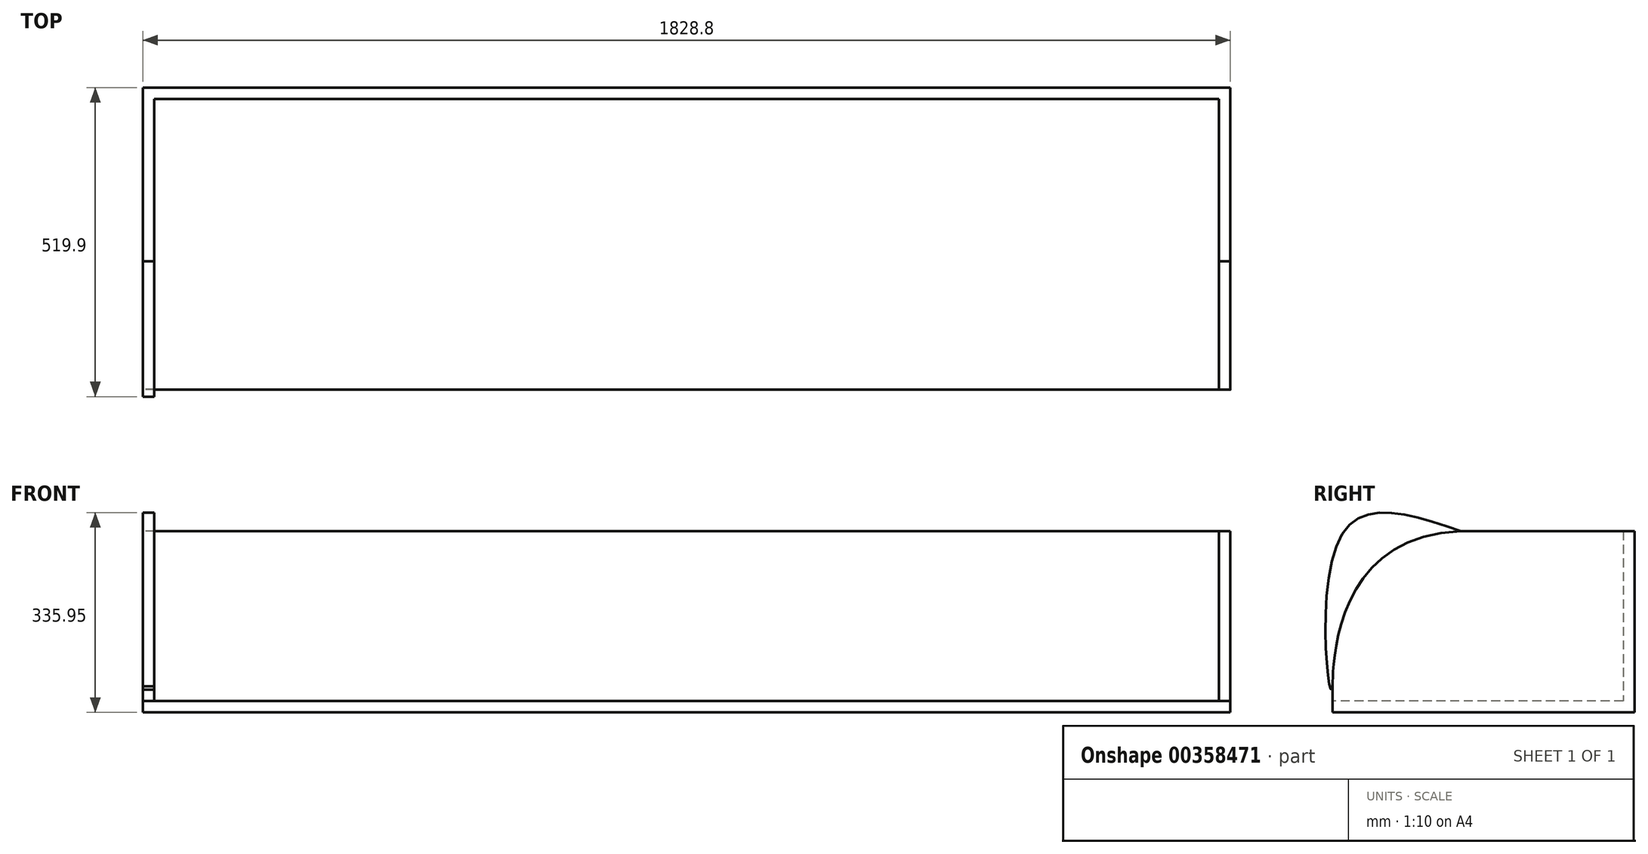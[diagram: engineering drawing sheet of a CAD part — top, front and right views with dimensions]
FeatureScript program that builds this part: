
annotation { "Feature Type Name" : "Feature", "Feature Type Description" : "" }
export const myFeature = defineFeature(function(context is Context, id is Id, definition is map)
    precondition{}
    {
        {
            var Q0;
            Q0=qCreatedBy(makeId("Right.planeOp"),FACE);
            var sketch = newSketch(context, id + "F0", { "sketchPlane" : qUnion([Q0])});
            skLineSegment(sketch, "E0", {"start": v(0, 0) * mm, "end": v(-508, 0) * mm});
            skLineSegment(sketch, "E1", {"start": v(-508, 0) * mm, "end": v(-508, 19.05) * mm});
            skLineSegment(sketch, "E2", {"start": v(-508, 19.05) * mm, "end": v(-19.05, 19.05) * mm});
            skLineSegment(sketch, "E3", {"start": v(-19.05, 19.05) * mm, "end": v(-19.05, 304.8) * mm});
            skLineSegment(sketch, "E4", {"start": v(-19.05, 304.8) * mm, "end": v(0, 304.8) * mm});
            skLineSegment(sketch, "E5", {"start": v(0, 304.8) * mm, "end": v(0, 0) * mm});
            skSolve(sketch);
        }
        {
            var Q0;
            Q0 = qSketchRegion(id + "F0", true);
            extrude(context, id + "F1", {"entities" : qUnion([Q0]), "depth" : 1828.8 * mm});
        }
        {
            var Q0;
            Q0=makeQuery(id+"F1.opExtrude","CAP_FACE",FACE,{"disambiguationData":[OSD([sQuery(id+"F0.wireOp",EDGE,"E0"),sQuery(id+"F0.wireOp",EDGE,"E1"),sQuery(id+"F0.wireOp",EDGE,"E2"),sQuery(id+"F0.wireOp",EDGE,"E3"),sQuery(id+"F0.wireOp",EDGE,"E4"),sQuery(id+"F0.wireOp",EDGE,"E5")])],"isStart":false});
            var sketch = newSketch(context, id + "F2", { "sketchPlane" : qUnion([Q0])});
            skLineSegment(sketch, "E6", {"start": v(-508, 0) * mm, "end": v(-508, 19.05) * mm});
            skLineSegment(sketch, "E7", {"start": v(-19.05, 304.8) * mm, "end": v(0, 304.8) * mm});
            skLineSegment(sketch, "E8", {"start": v(0, 304.8) * mm, "end": v(0, 0) * mm});
            skLineSegment(sketch, "E9", {"start": v(0, 0) * mm, "end": v(-508, 0) * mm});
            skLineSegment(sketch, "E10", {"start": v(-19.05, 304.8) * mm, "end": v(-292, 304.8) * mm});
            skFitSpline(sketch, "E11", {"points": [v(-292, 304.8) * mm, v(-507.49, 58) * mm, v(-508, 19.05) * mm], "startDerivative": vector(-810.8, -27.33) * mm, "endDerivative": vector(-5.98, -284.64) * mm});
            skSolve(sketch);
        }
        {
            var Q0;
            Q0 = qSketchRegion(id + "F2", true);
            extrude(context, id + "F3", {"entities" : qUnion([Q0]), "operationType" : NewBodyOperationType.ADD, "oppositeDirection" : true, "depth" : 19.05 * mm});
        }
        {
            var Q0;
            Q0=makeQuery(id+"F1.opExtrude","CAP_FACE",FACE,{"disambiguationData":[OSD([sQuery(id+"F0.wireOp",EDGE,"E0"),sQuery(id+"F0.wireOp",EDGE,"E1"),sQuery(id+"F0.wireOp",EDGE,"E2"),sQuery(id+"F0.wireOp",EDGE,"E3"),sQuery(id+"F0.wireOp",EDGE,"E4"),sQuery(id+"F0.wireOp",EDGE,"E5")])],"isStart":true});
            var sketch = newSketch(context, id + "F4", { "sketchPlane" : qUnion([Q0])});
            skLineSegment(sketch, "E12", {"start": v(0, 304.8) * mm, "end": v(19.05, 304.8) * mm});
            skLineSegment(sketch, "E13", {"start": v(508, 19.05) * mm, "end": v(508, 0) * mm});
            skLineSegment(sketch, "E14", {"start": v(508, 0) * mm, "end": v(0, 0) * mm});
            skLineSegment(sketch, "E15", {"start": v(0, 0) * mm, "end": v(0, 304.8) * mm});
            skFitSpline(sketch, "E16.0", {"points": [v(292, 304.8) * mm, v(492.98, 298.03) * mm, v(510, 37.81) * mm, v(507.49, 43.38) * mm, v(508, 19.05) * mm]});
            skLineSegment(sketch, "E16.1", {"start": v(292, 304.8) * mm, "end": v(19.05, 304.8) * mm});
            skSolve(sketch);
        }
        {
            var Q0;
            Q0 = qSketchRegion(id + "F4", true);
            extrude(context, id + "F5", {"entities" : qUnion([Q0]), "operationType" : NewBodyOperationType.ADD, "oppositeDirection" : true, "depth" : 19.05 * mm});
        }
    });
